# Revit family: 94700401
name_source: partatom
category: Modelos genéricos
revit_build: Autodesk Revit 2016 (Build: 20150220_1215(x64)
units: mm (PartAtom-declared; Revit-internal decimal feet)

## family parameters
Com base no plano de trabalho = Não
Compartilhado = Não
Corte com vazios quando carregados = Não
Cota do conector redondo = Utilizar diâmetro
Pode hospedar o vergalhão = Não
Ponto de cálculo do ambiente = Não
Sempre na vertical = Sim
Tipo de parte = Normal

## types (1)
- Cooktop Domino Tramontina
    Acabamento = Scotch brite
    Código de montagem = Cooktop Tramontina - Dominó - 94700401
    Descrição = Cooktop Tramontina - Dominó - 94700401
    Desenvolvedor = Factory Cursos & Desenvolvimento
    Eficiência Energética = A
    Fabricante = Tramontina
    Frequencia = 50 - 60 Hz
    Material = Aço Inox AISI 430
    Potência Termica Total = 4,2 kW
    Referencia = Cooktop Tramontina - Dominó - 94700401
    Site do desenvolvedor = www.factorycursos.com.br
    Tampa = Sim
    Tensão = 127 - 220V
    Tipo de imagem = <Nenhum>
    Tratamento anti digitais = Não
    URL = www.tramontina.com.br
